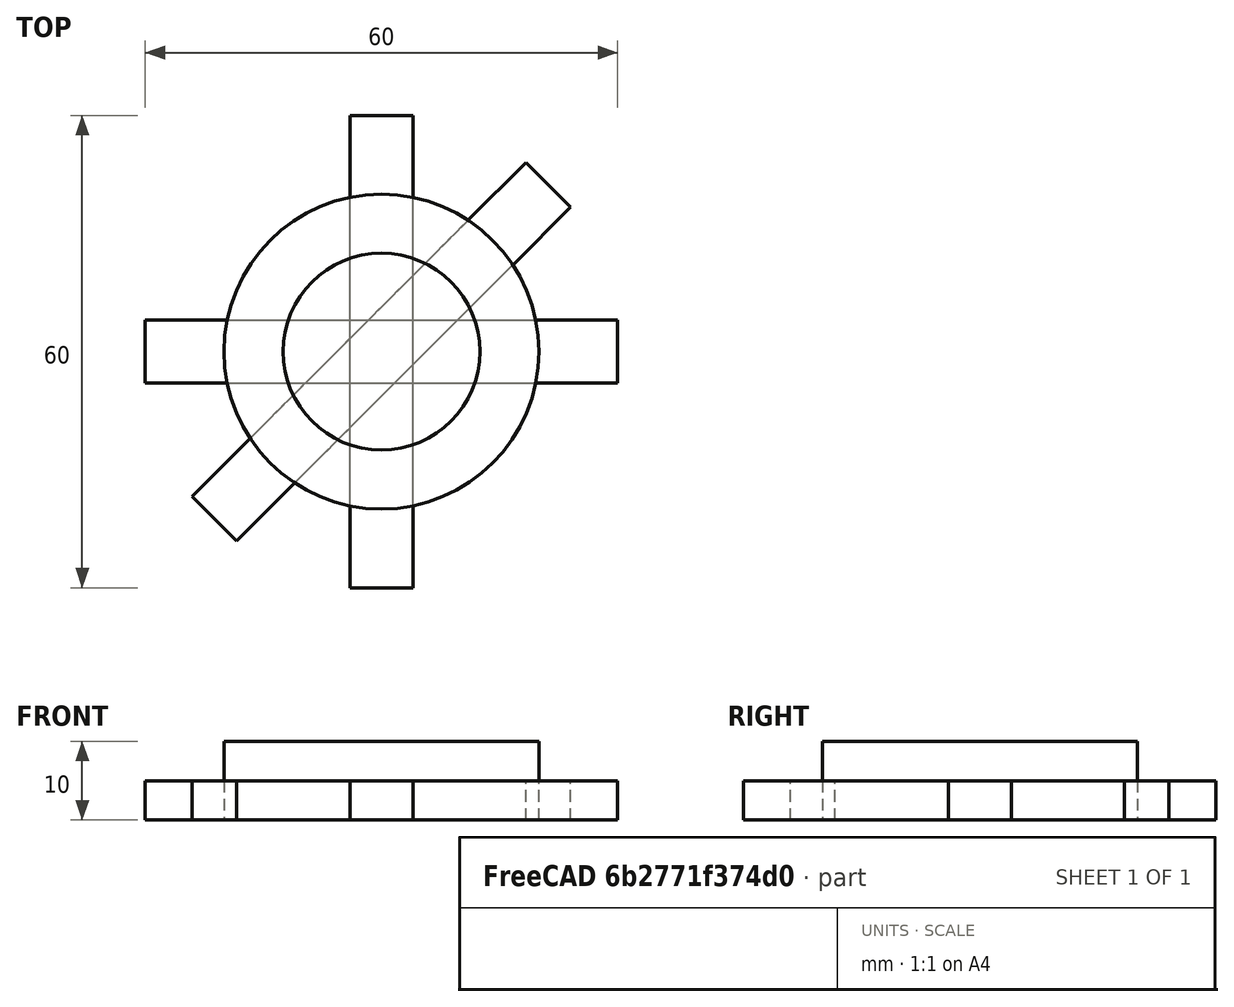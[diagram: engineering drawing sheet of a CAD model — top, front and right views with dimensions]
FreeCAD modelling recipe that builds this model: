
FCSTD DOCUMENT  (FreeCAD 0.20R29177 +426 (Git))
Label: Engranaje
License: All rights reserved
LicenseURL: http://en.wikipedia.org/wiki/All_rights_reserved
objects: Part::Box×4, Part::Cylinder×2
note: 6 computed .brp shape members not serialized (recipe doc carries the construction recipe); baked Part::Feature solids carry a one-line shape summary decoded from their .brp

FEATURE [Part::Box] Box  label="Cubo"
  AttacherType = Attacher::AttachEngine3D
  Height = 5
  Length = 60
  Placement = pos=(-30,-4,0) rot=(0,0,1;0rad)
  Width = 8
FEATURE [Part::Box] Box001  label="Cubo001"
  AttacherType = Attacher::AttachEngine3D
  Height = 5
  Length = 60
  Placement = pos=(-18.3848,-24.0416,0) rot=(0,0,1;0.785398rad)
  Width = 8
FEATURE [Part::Box] Box002  label="Cubo002"
  AttacherType = Attacher::AttachEngine3D
  Height = 5
  Length = 60
  Placement = pos=(-24.0416,18.3848,0) rot=(0,0,1;-0.785398rad)
  Width = 8
FEATURE [Part::Box] Box003  label="Cubo003"
  AttacherType = Attacher::AttachEngine3D
  Height = 5
  Length = 60
  Placement = pos=(4,-30,0) rot=(0,0,1;1.5708rad)
  Width = 8
FEATURE [Part::Cylinder] Cylinder  label="Cilindro"
  Angle = 360
  AttacherType = Attacher::AttachEngine3D
  FirstAngle = 0
  Height = 10
  Radius = 20
  SecondAngle = 0
FEATURE [Part::Cylinder] Cylinder001  label="Cilindro001"
  Angle = 360
  AttacherType = Attacher::AttachEngine3D
  FirstAngle = 0
  Height = 10
  Radius = 12.5
  SecondAngle = 0
